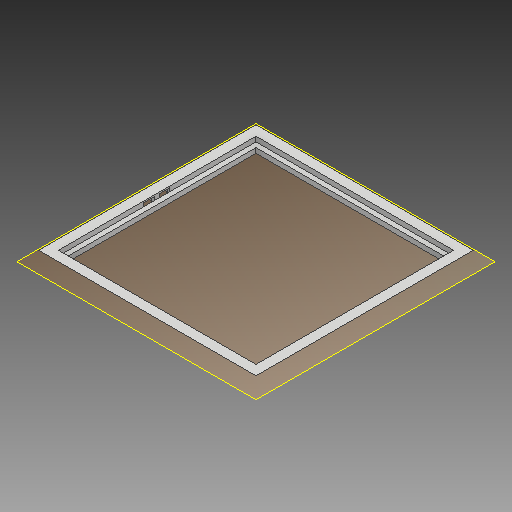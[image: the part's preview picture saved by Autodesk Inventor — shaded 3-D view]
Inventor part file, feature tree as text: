
AUTODESK INVENTOR PART (.ipt)
format: ipt  version: 2018.2 (Build 222227000, 227)  size: 142,848 bytes
history: native  units: mm
features: reference x13, other x7, extrude x3, sketch x3, chamfer x1, plane x1
ambient origin geometry x8: Origin, YZ Plane, XZ Plane, XY Plane, X Axis, Y Axis, Z Axis, Center Point
bodies: Volumenkörper1 (feature_tree)
feature tree (28):
  extrude  "Extrusion1"  Depth=20.0mm TaperAngle=45.0deg
  chamfer  "Fase1"  Distance=17.0mm
  plane  "Arbeitsebene1"
  extrude  "Extrusion2"  Depth=10.0mm
  extrude  "Extrusion3"  Depth=10.0mm
  sketch  "Skizze1"  dims[d0=20.0mm d1=0.0mm d2=20.0mm d3=2.0mm d4=45.0deg]
  reference  "Referenz1"
  reference  "Referenz2"
  reference  "Referenz3"
  reference  "Referenz4"
  reference  "Referenz5"
  sketch  "Skizze3"  dims[d5=-20.0mm d6=17.0mm d7=0.0mm]
  reference  "Referenz12"
  reference  "Referenz13"
  reference  "Referenz14"
  reference  "Referenz15"
  reference  "Referenz16"
  reference  "Referenz17"
  reference  "Referenz18"
  reference  "Referenz19"
  sketch  "Skizze5"  dims[d8=10.0mm d9=10.0mm d10=10.0mm d11=10.0mm d12=10.0mm d13=0.0mm]
  parser-record x1  (decoder bookkeeping rows leaked as tree rows — omitted from the tree; the rows remain in map.json)
  other  "SmartCube_Quadratisch.iam"
  other  "Wand2_MIR:1"
  other  "Wand1:1"
  other  "Wand1_MIR:1"
  other  "Wand2:1"
  other  "PV_Modul:1"
note: 1 file-system path scrubbed to <path> (originals preserved in map.json)
